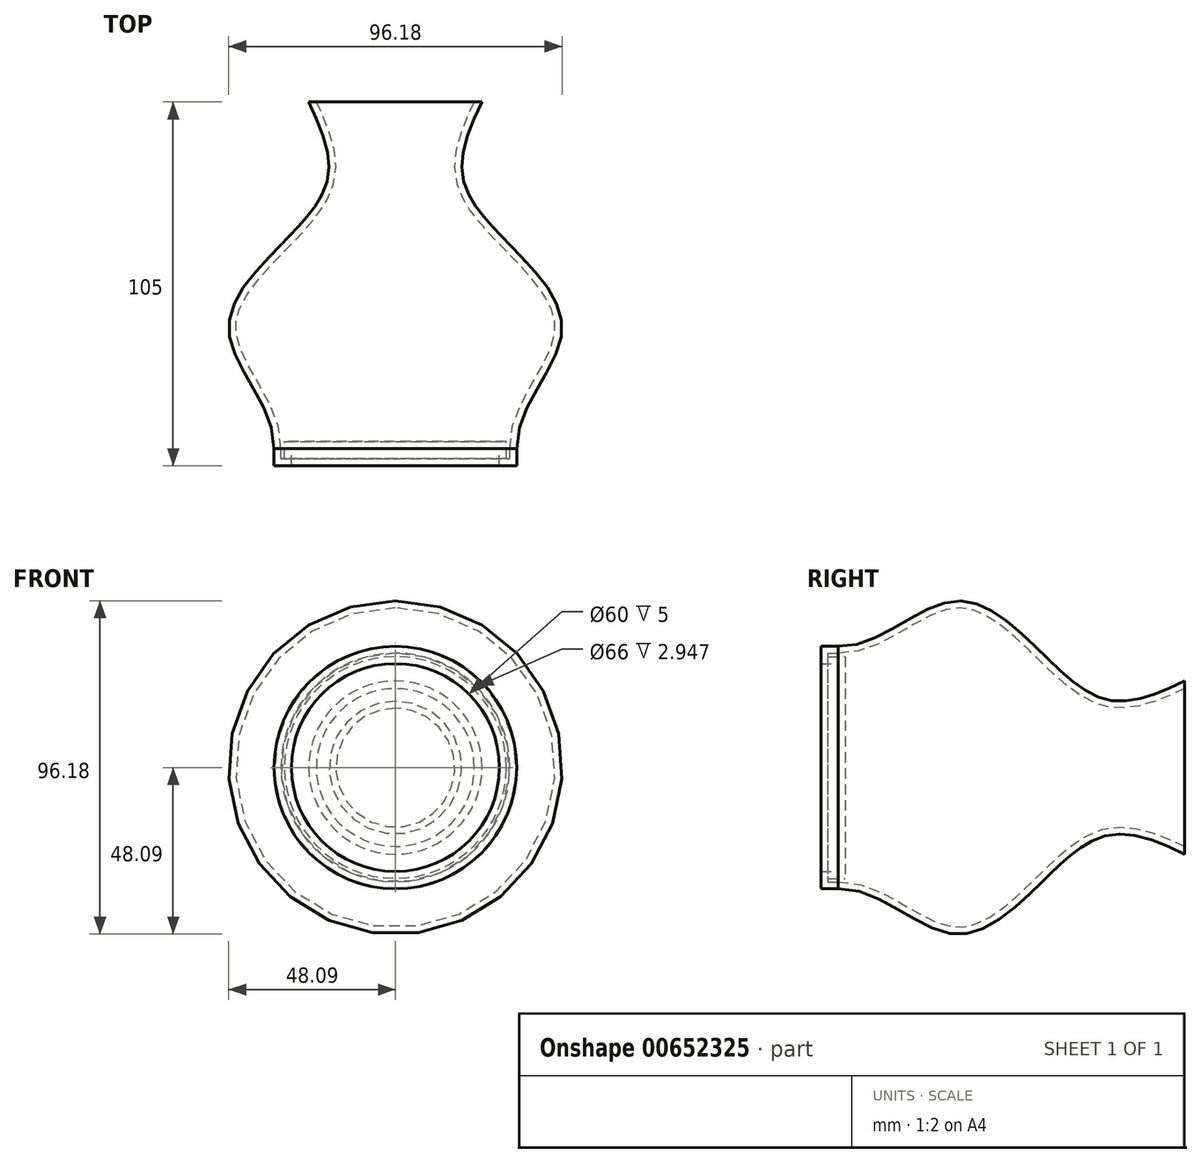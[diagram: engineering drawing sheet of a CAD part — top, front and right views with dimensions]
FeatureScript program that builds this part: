
annotation { "Feature Type Name" : "Feature", "Feature Type Description" : "" }
export const myFeature = defineFeature(function(context is Context, id is Id, definition is map)
    precondition{}
    {
        {
            var Q0;
            Q0=qCreatedBy(makeId("Top.planeOp"),FACE);
            var sketch = newSketch(context, id + "F0", { "sketchPlane" : qUnion([Q0])});
            skLineSegment(sketch, "E0", {"start": v(25, 80.2) * mm, "end": v(0, 80.2) * mm});
            skLineSegment(sketch, "E1", {"start": v(0, 80.2) * mm, "end": v(0, -19.8) * mm});
            skLineSegment(sketch, "E2", {"start": v(0, -19.8) * mm, "end": v(30, -19.8) * mm});
            skLineSegment(sketch, "E3", {"start": v(30, -19.8) * mm, "end": v(30, -24.8) * mm});
            skLineSegment(sketch, "E4", {"start": v(30, -24.8) * mm, "end": v(35, -24.8) * mm});
            skLineSegment(sketch, "E5", {"start": v(35, -24.8) * mm, "end": v(35, -19.8) * mm});
            skFitSpline(sketch, "E6", {"points": [v(25, 80.2) * mm, v(19.4, 58.55) * mm, v(33.37, 38.6) * mm, v(48, 13.33) * mm, v(35, -19.8) * mm], "startDerivative": vector(-48.13, -100.22) * mm, "endDerivative": vector(6.67, -121.92) * mm});
            skSolve(sketch);
        }
        {
            var Q0;
            Q0 = qSketchRegion(id + "F0", true);
            var Q1;
            Q1=sQuery(id+"F0.wireOp",EDGE,"E1");
            revolve(context, id + "F1", {"surfaceOperationType" : NewSurfaceOperationType.NEW, "entities" : qUnion([Q0]), "axis" : qUnion([Q1]), "revolveType" : RevolveType.FULL});
        }
        {
            var Q0;
            Q0=makeQuery(id+"F1.opRevolve","SWEPT_FACE",FACE,{"disambiguationData":[OSD([sQuery(id+"F0.wireOp",EDGE,"E0")])]});
            shell(context, id + "F2", {"entities" : qUnion([Q0]), "thickness" : 2 * mm});
        }
    });
